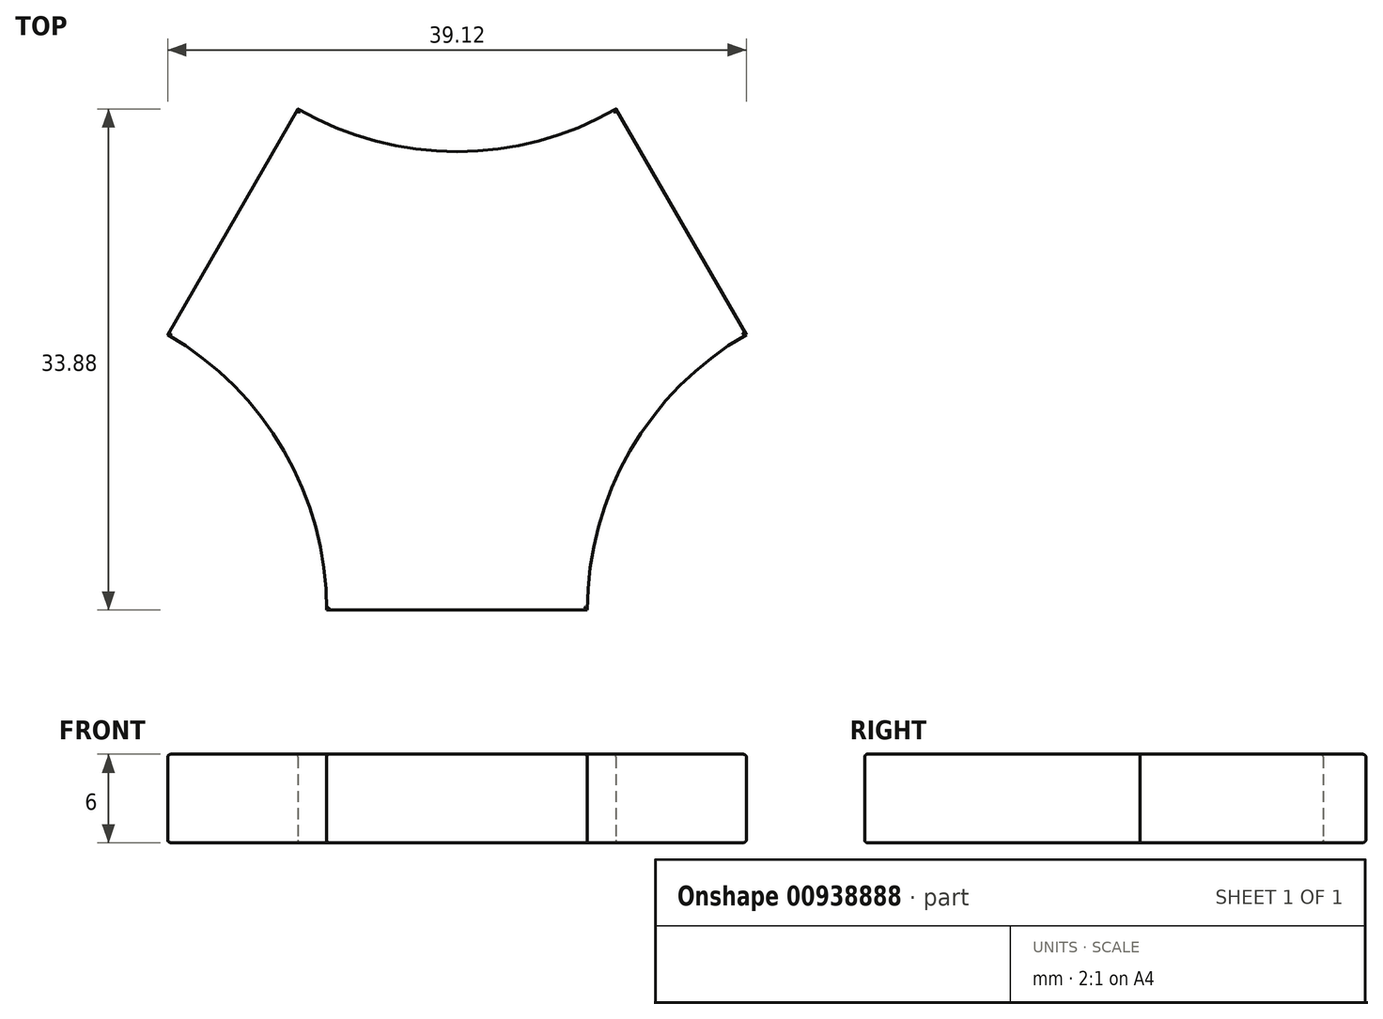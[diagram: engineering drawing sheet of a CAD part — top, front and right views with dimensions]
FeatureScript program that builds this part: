
annotation { "Feature Type Name" : "Feature", "Feature Type Description" : "" }
export const myFeature = defineFeature(function(context is Context, id is Id, definition is map)
    precondition{}
    {
        {
            var Q0;
            Q0=qCreatedBy(makeId("Top.planeOp"),FACE);
            var sketch = newSketch(context, id + "F0", { "sketchPlane" : qUnion([Q0])});
            skLineSegment(sketch, "E0.0", {"start": v(10.75, 16.38) * mm, "end": v(19.56, 1.12) * mm});
            skLineSegment(sketch, "E0.1", {"start": v(8.81, -17.5) * mm, "end": v(-8.81, -17.5) * mm});
            skLineSegment(sketch, "E0.2", {"start": v(-19.56, 1.12) * mm, "end": v(-10.75, 16.38) * mm});
            skArc(sketch, "E1", {"start": v(19.56, 1.12) * mm, "mid": v(11.7, -6.75) * mm, "end": v(8.81, -17.5) * mm});
            skArc(sketch, "E2", {"start": v(-8.81, -17.5) * mm, "mid": v(-11.7, -6.75) * mm, "end": v(-19.56, 1.12) * mm});
            skPoint(sketch, "E0.cCircle.center.orphan", {"position": v(0, 0) * mm});
            skArc(sketch, "E3.trimOffspring", {"start": v(-10.75, 16.38) * mm, "mid": v(0, 13.5) * mm, "end": v(10.75, 16.38) * mm});
            skSolve(sketch);
        }
        {
            var Q0;
            Q0=makeQuery(id+"F0.imprint","IMPRINT",FACE,{"disambiguationData":[TD([[makeQuery(id+"F0.imprint","IMPRINT",EDGE,{"derivedFrom":sQuery(id+"F0.wireOp",EDGE,"E0.0")}),-1.0]])]});
            extrude(context, id + "F1", {"entities" : qUnion([Q0]), "depth" : 6 * mm, "offsetDistance" : 25 * mm});
        }
        {
            var Q0;
            Q0=makeQuery(id+"F1.opExtrude","CAP_FACE",FACE,{"disambiguationData":[OSD([sQuery(id+"F0.wireOp",EDGE,"E0.0"),sQuery(id+"F0.wireOp",EDGE,"E0.1"),sQuery(id+"F0.wireOp",EDGE,"E0.2"),sQuery(id+"F0.wireOp",EDGE,"E1"),sQuery(id+"F0.wireOp",EDGE,"E2"),sQuery(id+"F0.wireOp",EDGE,"E3.trimOffspring")])],"isStart":false});
            var Q1;
            Q1=makeQuery(id+"F1.opExtrude","CAP_FACE",FACE,{"disambiguationData":[OSD([sQuery(id+"F0.wireOp",EDGE,"E0.0"),sQuery(id+"F0.wireOp",EDGE,"E0.1"),sQuery(id+"F0.wireOp",EDGE,"E0.2"),sQuery(id+"F0.wireOp",EDGE,"E1"),sQuery(id+"F0.wireOp",EDGE,"E2"),sQuery(id+"F0.wireOp",EDGE,"E3.trimOffspring")])],"isStart":true});
            fillet(context, id + "F2", {"entities" : qUnion([Q0, Q1]), "radius" : 0.2 * mm, "tangentPropagation" : true, "allowEdgeOverflow" : false});
        }
    });
